# Revit family: rba-bim-B2012
name_source: partatom
category: Specialty Equipment
revit_build: Autodesk Revit 2018 (Build: 20170223_1515(x64)
units: mm (PartAtom-declared; Revit-internal decimal feet)

## family parameters
Always vertical = Yes
Cut with Voids When Loaded = No
Part Type = Normal
Room Calculation Point = No
Round Connector Dimension = Use Diameter
Shared = Yes
Work Plane-Based = No

## types (1)
- B2012
    Description = Automatic Wall Mounted Liquid Soap Dispenser
    Diameter = 32 mm  [stored 0.104987 ft]
    Lgth = 900 mm  [stored 2.95276 ft]
    Manufacturer = Bobrick Washroom Equipment, Inc.
    Materials and Finishes = Stainless Steel - Satin
    Model = RBA-B2012
    Modified Issue = 20200323.01
    URL = http://www.bobrick.com

note: [stored X ft] marks values corroborated as IEEE doubles in the binary element streams (Revit-internal decimal feet)

## geometry (parser evidence)
native form markers: Blend x6, Sweep x3
no freeform markers — native parametric forms only
